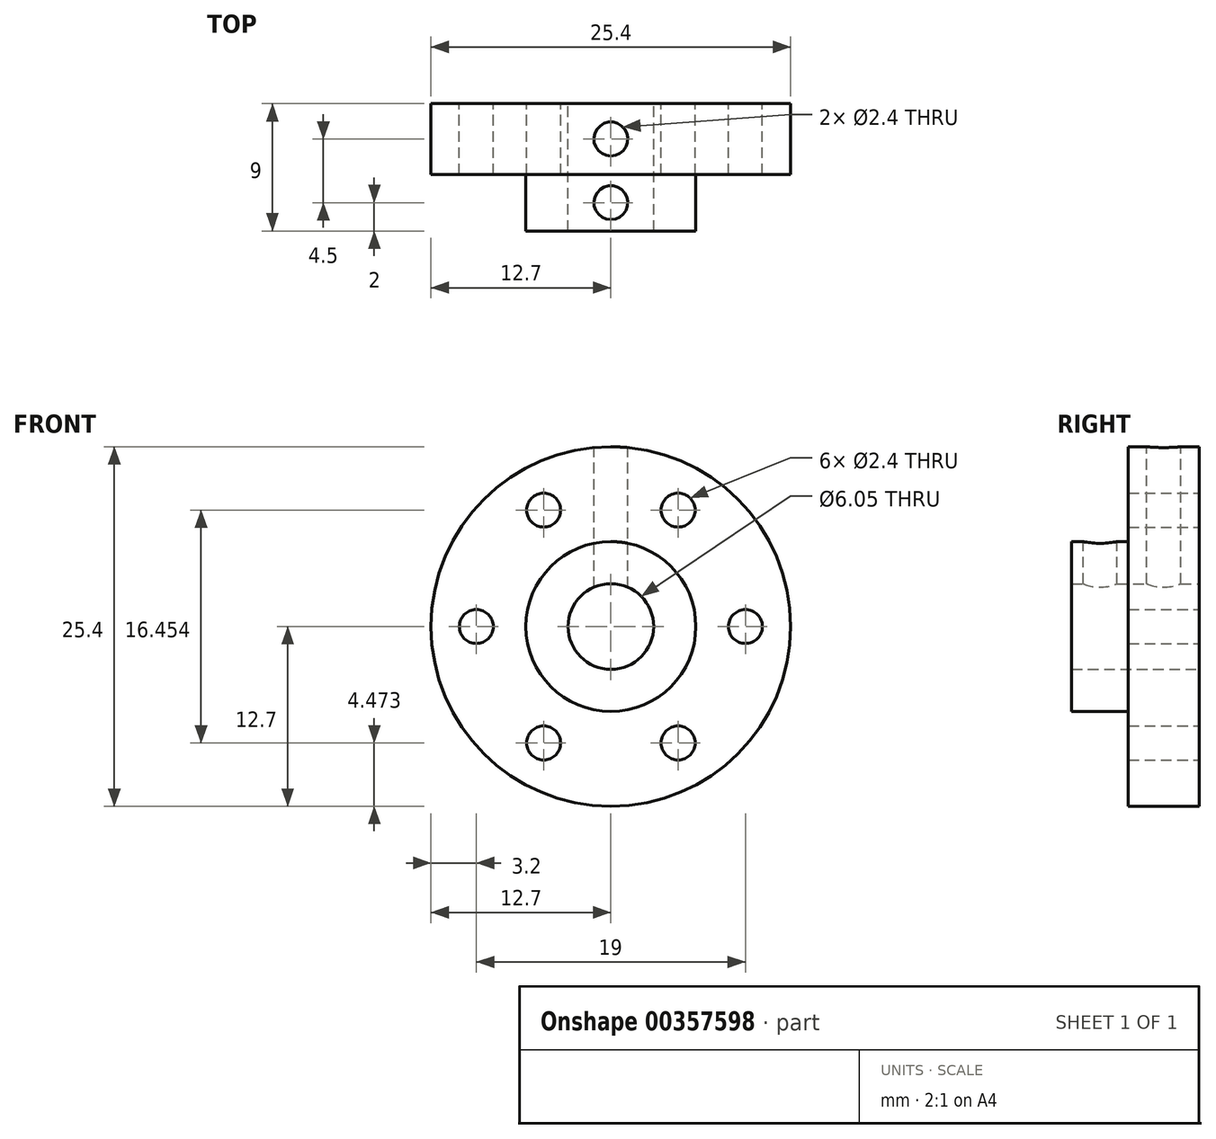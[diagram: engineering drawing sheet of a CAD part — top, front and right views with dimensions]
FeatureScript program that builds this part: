
annotation { "Feature Type Name" : "Feature", "Feature Type Description" : "" }
export const myFeature = defineFeature(function(context is Context, id is Id, definition is map)
    precondition{}
    {
        {
            var Q0;
            Q0=qCreatedBy(makeId("Front.planeOp"),FACE);
            var sketch = newSketch(context, id + "F0", { "sketchPlane" : qUnion([Q0])});
            skCircle(sketch, "E0", {"center": v(0, 0) * mm, "radius": 12.7 * mm});
            skCircle(sketch, "E1", {"center": v(0, 0) * mm, "radius": 6 * mm});
            skCircle(sketch, "E2", {"center": v(0, 0) * mm, "radius": 3.02 * mm});
            skLineSegment(sketch, "E3", {"start": v(0, 0) * mm, "end": v(9.5, 0) * mm, "construction": true});
            skLineSegment(sketch, "E4.1.0", {"start": v(0, 0) * mm, "end": v(4.75, 8.23) * mm, "construction": true});
            skLineSegment(sketch, "E4.2.0", {"start": v(0, 0) * mm, "end": v(-4.75, 8.23) * mm, "construction": true});
            skLineSegment(sketch, "E4.3.0", {"start": v(0, 0) * mm, "end": v(-9.5, 0) * mm, "construction": true});
            skLineSegment(sketch, "E4.4.0", {"start": v(0, 0) * mm, "end": v(-4.75, -8.23) * mm, "construction": true});
            skLineSegment(sketch, "E4.5.0", {"start": v(0, 0) * mm, "end": v(4.75, -8.23) * mm, "construction": true});
            skSolve(sketch);
        }
        {
            var Q0;
            Q0=makeQuery(id+"F0.imprint","IMPRINT",FACE,{"disambiguationData":[TD([[makeQuery(id+"F0.imprint","IMPRINT",EDGE,{"derivedFrom":sQuery(id+"F0.wireOp",EDGE,"E1")}),1.0]])]});
            var Q1;
            Q1=makeQuery(id+"F0.imprint","IMPRINT",FACE,{"disambiguationData":[TD([[makeQuery(id+"F0.imprint","IMPRINT",EDGE,{"derivedFrom":sQuery(id+"F0.wireOp",EDGE,"E0")}),1.0]])]});
            extrude(context, id + "F1", {"entities" : qUnion([Q0, Q1]), "depth" : 5 * mm});
        }
        {
            var Q0;
            Q0=makeQuery(id+"F0.imprint","IMPRINT",FACE,{"disambiguationData":[TD([[makeQuery(id+"F0.imprint","IMPRINT",EDGE,{"derivedFrom":sQuery(id+"F0.wireOp",EDGE,"E1")}),1.0]])]});
            extrude(context, id + "F2", {"entities" : qUnion([Q0]), "operationType" : NewBodyOperationType.ADD, "depth" : 9 * mm});
        }
        {
            var Q0;
            Q0=sQuery(id+"F0.wireOp",VERTEX,"E3.end");
            var Q1;
            Q1=sQuery(id+"F0.wireOp",VERTEX,"E4.1.0.end");
            var Q2;
            Q2=sQuery(id+"F0.wireOp",VERTEX,"E4.2.0.end");
            var Q3;
            Q3=sQuery(id+"F0.wireOp",VERTEX,"E4.3.0.end");
            var Q4;
            Q4=sQuery(id+"F0.wireOp",VERTEX,"E4.4.0.end");
            var Q5;
            Q5=sQuery(id+"F0.wireOp",VERTEX,"E4.5.0.end");
            var Q6;
            Q6=makeQuery(id+"F1.opExtrude","SWEPT_BODY",BODY,{"disambiguationData":[OSD([sQuery(id+"F0.wireOp",EDGE,"E0"),sQuery(id+"F0.wireOp",EDGE,"E2")])]});
            hole(context, id + "F3", {"style" : HoleStyle.SIMPLE, "endStyle" : HoleEndStyle.THROUGH, "oppositeDirection" : true, "standardTappedOrClearance" : lookupTablePath({ "standard" : "ISO", "engagement" : "75%", "pitch" : "0.6 mm", "size" : "M3", "type" : "Tapped" }), "standardBlindInLast" : lookupTablePath({ "standard" : "ISO", "engagement" : "75%", "pitch" : "0.6 mm", "size" : "M3", "type" : "Tapped" }), "holeDiameter" : 2.4 * mm, "showTappedDepth" : true, "tappedDepth" : 5 * mm, "tapClearance" : 3, "locations" : qUnion([Q0, Q1, Q2, Q3, Q4, Q5]), "scope" : qUnion([Q6])});
        }
        {
            var Q0;
            Q0=qCreatedBy(makeId("Top.planeOp"),FACE);
            cPlane(context, id + "F4", {"entities" : qUnion([Q0]), "cplaneType" : CPlaneType.OFFSET, "offset" : (25.4 / 2) * mm, "width" : 150 * mm, "height" : 150 * mm});
        }
        {
            var Q0;
            Q0=qCreatedBy(id+"F4.planeOp",FACE);
            var sketch = newSketch(context, id + "F5", { "sketchPlane" : qUnion([Q0])});
            skLineSegment(sketch, "E5", {"start": v(12.7, 0) * mm, "end": v(12.7, -5) * mm, "construction": true});
            skLineSegment(sketch, "E6", {"start": v(-12.7, -5) * mm, "end": v(-12.7, 0) * mm, "construction": true});
            skLineSegment(sketch, "E7", {"start": v(0, 0) * mm, "end": v(0, -5) * mm, "construction": true});
            skPoint(sketch, "E8", {"position": v(0, -2.5) * mm});
            skLineSegment(sketch, "E9", {"start": v(6, -5) * mm, "end": v(6, -9) * mm, "construction": true});
            skLineSegment(sketch, "E10", {"start": v(-6, -9) * mm, "end": v(-6, -5) * mm, "construction": true});
            skLineSegment(sketch, "E11", {"start": v(0, -5) * mm, "end": v(0, -9) * mm, "construction": true});
            skPoint(sketch, "E12", {"position": v(0, -7) * mm});
            skSolve(sketch);
        }
        {
            var Q0;
            Q0=sQuery(id+"F5.wireOp",VERTEX,"E8");
            var Q1;
            Q1=sQuery(id+"F5.wireOp",VERTEX,"E12");
            var Q2;
            Q2=makeQuery(id+"F1.opExtrude","SWEPT_BODY",BODY,{"disambiguationData":[OSD([sQuery(id+"F0.wireOp",EDGE,"E0"),sQuery(id+"F0.wireOp",EDGE,"E2")])]});
            hole(context, id + "F6", {"style" : HoleStyle.SIMPLE, "endStyle" : HoleEndStyle.BLIND, "standardTappedOrClearance" : lookupTablePath({ "standard" : "ISO", "engagement" : "75%", "pitch" : "0.6 mm", "size" : "M3", "type" : "Tapped" }), "standardBlindInLast" : lookupTablePath({ "standard" : "ISO", "engagement" : "75%", "pitch" : "0.6 mm", "size" : "M3", "type" : "Tapped" }), "holeDiameter" : 2.4 * mm, "showTappedDepth" : true, "holeDepth" : 10 * mm, "tappedDepth" : 8.2 * mm, "tapClearance" : 3, "startFromSketch" : true, "locations" : qUnion([Q0, Q1]), "scope" : qUnion([Q2])});
        }
    });
